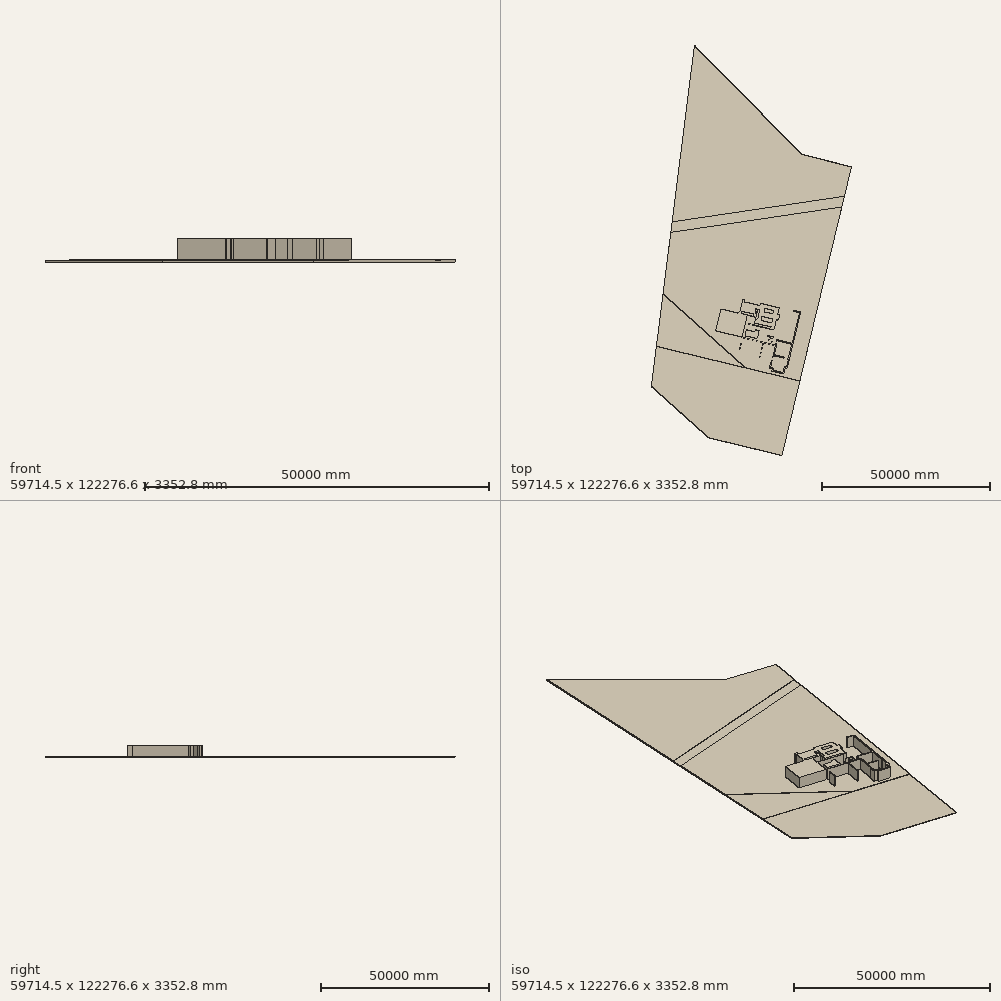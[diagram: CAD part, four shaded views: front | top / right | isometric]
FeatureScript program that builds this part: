
annotation { "Feature Type Name" : "Feature", "Feature Type Description" : "" }
export const myFeature = defineFeature(function(context is Context, id is Id, definition is map)
    precondition{}
    {
        {
            var Q0;
            Q0=qCreatedBy(makeId("Top.planeOp"),FACE);
            var sketch = newSketch(context, id + "F0", { "sketchPlane" : qUnion([Q0])});
            skLineSegment(sketch, "E0", {"start": v(0, 0) * mm, "end": v(31989.83, -32467.96) * mm});
            skLineSegment(sketch, "E1", {"start": v(31989.83, -32467.96) * mm, "end": v(46862.18, -36229.17) * mm});
            skLineSegment(sketch, "E2", {"start": v(46862.18, -36229.17) * mm, "end": v(26112.23, -122276.56) * mm});
            skLineSegment(sketch, "E3", {"start": v(46862.18, -36229.17) * mm, "end": v(46862.18, -51469.17) * mm, "construction": true});
            skLineSegment(sketch, "E4", {"start": v(0, 0) * mm, "end": v(-12852.3, -101676.89) * mm});
            skLineSegment(sketch, "E5", {"start": v(0, 0) * mm, "end": v(0, 15240) * mm, "construction": true});
            skLineSegment(sketch, "E6", {"start": v(26112.23, -122276.56) * mm, "end": v(4230, -116999.76) * mm});
            skLineSegment(sketch, "E7", {"start": v(26112.23, -122276.56) * mm, "end": v(10872.23, -122276.56) * mm, "construction": true});
            skLineSegment(sketch, "E8", {"start": v(4230, -116999.76) * mm, "end": v(-12852.3, -101676.89) * mm});
            skArc(sketch, "E9", {"start": v(-4165.07, -109469.35) * mm, "mid": v(-689.73, -114039.67) * mm, "end": v(4230, -116999.76) * mm, "construction": true});
            skArc(sketch, "E10", {"start": v(-4165.07, -109469.35) * mm, "mid": v(-8132.26, -105153.47) * mm, "end": v(-12852.3, -101676.89) * mm, "construction": true});
            skLineSegment(sketch, "E11", {"start": v(31471.2, -100053.58) * mm, "end": v(-11342.08, -89729.35) * mm});
            skLineSegment(sketch, "E12", {"start": v(-9365.85, -74095.03) * mm, "end": v(15198.72, -96129.54) * mm});
            skLineSegment(sketch, "E13", {"start": v(-6651.63, -52622.31) * mm, "end": v(44754.67, -44968.73) * mm});
            skLineSegment(sketch, "E14", {"start": v(-7048.63, -55763.02) * mm, "end": v(43983.88, -48165.09) * mm});
            skSolve(sketch);
        }
        {
            var Q0;
            {var subQ4=sQuery(id+"F0.wireOp",EDGE,"E0");Q0=makeQuery(id+"F0.imprint","IMPRINT",FACE,{"disambiguationData":[TD([[makeQuery(id+"F0.imprint","IMPRINT",EDGE,{"derivedFrom":subQ4}),-1.0]])]});}
            var Q1;
            {var subQ0=sQuery(id+"F0.wireOp",EDGE,"E13");Q1=makeQuery(id+"F0.imprint","IMPRINT",FACE,{"disambiguationData":[TD([[makeQuery(id+"F0.imprint","IMPRINT",EDGE,{"derivedFrom":subQ0}),-1.0]])]});}
            var Q2;
            {var subQ0=sQuery(id+"F0.wireOp",EDGE,"E12");Q2=makeQuery(id+"F0.imprint","IMPRINT",FACE,{"disambiguationData":[TD([[makeQuery(id+"F0.imprint","IMPRINT",EDGE,{"derivedFrom":subQ0}),1.0]])]});}
            var Q3;
            {var subQ3=sQuery(id+"F0.wireOp",EDGE,"E12");Q3=makeQuery(id+"F0.imprint","IMPRINT",FACE,{"disambiguationData":[TD([[makeQuery(id+"F0.imprint","IMPRINT",EDGE,{"derivedFrom":subQ3}),-1.0]])]});}
            var Q4;
            {var subQ1=sQuery(id+"F0.wireOp",EDGE,"E6");Q4=makeQuery(id+"F0.imprint","IMPRINT",FACE,{"disambiguationData":[TD([[makeQuery(id+"F0.imprint","IMPRINT",EDGE,{"derivedFrom":subQ1}),-1.0]])]});}
            extrude(context, id + "F1", {"entities" : qUnion([Q0, Q1, Q2, Q3, Q4]), "depth" : 304.8 * mm, "offsetDistance" : 25.4 * mm});
        }
        {
            var Q0;
            Q0=makeQuery(id+"F1.opExtrude","CAP_FACE",FACE,{"disambiguationData":[OSD([sQuery(id+"F0.wireOp",EDGE,"E0"),sQuery(id+"F0.wireOp",EDGE,"E1"),sQuery(id+"F0.wireOp",EDGE,"E2"),sQuery(id+"F0.wireOp",EDGE,"E4"),sQuery(id+"F0.wireOp",EDGE,"E6"),sQuery(id+"F0.wireOp",EDGE,"E8")])],"isStart":false});
            var sketch = newSketch(context, id + "F2", { "sketchPlane" : qUnion([Q0])});
            skLineSegment(sketch, "E15.0", {"start": v(-9365.85, -74095.03) * mm, "end": v(15198.72, -96129.54) * mm});
            skLineSegment(sketch, "E16.0", {"start": v(31471.2, -100053.58) * mm, "end": v(-11342.08, -89729.35) * mm});
            skLineSegment(sketch, "E17.0", {"start": v(0, 0) * mm, "end": v(-12852.3, -101676.89) * mm});
            skSolve(sketch);
        }
        {
            var Q0;
            {var subQ0=sQuery(id+"F2.wireOp",EDGE,"E15.0");Q0=makeQuery(id+"F2.imprint","IMPRINT",FACE,{"disambiguationData":[TD([[makeQuery(id+"F2.imprint","IMPRINT",EDGE,{"derivedFrom":subQ0}),-1.0]])]});}
            extrude(context, id + "F3", {"entities" : qUnion([Q0]), "operationType" : NewBodyOperationType.REMOVE, "oppositeDirection" : true, "depth" : 76.2 * mm, "offsetDistance" : 25.4 * mm});
        }
        {
            var Q0;
            Q0=makeQuery(id+"F1.opExtrude","CAP_FACE",FACE,{"disambiguationData":[OSD([sQuery(id+"F0.wireOp",EDGE,"E0"),sQuery(id+"F0.wireOp",EDGE,"E1"),sQuery(id+"F0.wireOp",EDGE,"E2"),sQuery(id+"F0.wireOp",EDGE,"E4"),sQuery(id+"F0.wireOp",EDGE,"E6"),sQuery(id+"F0.wireOp",EDGE,"E8")])],"isStart":false});
            var sketch = newSketch(context, id + "F4", { "sketchPlane" : qUnion([Q0])});
            skLineSegment(sketch, "E18.0", {"start": v(0, 0) * mm, "end": v(-12852.3, -101676.89) * mm});
            skLineSegment(sketch, "E19.0", {"start": v(4230, -116999.76) * mm, "end": v(-12852.3, -101676.89) * mm});
            skLineSegment(sketch, "E20.0", {"start": v(26112.23, -122276.56) * mm, "end": v(4230, -116999.76) * mm});
            skLineSegment(sketch, "E21.0", {"start": v(46862.18, -36229.17) * mm, "end": v(26112.23, -122276.56) * mm});
            skLineSegment(sketch, "E22.0", {"start": v(31471.2, -100053.58) * mm, "end": v(-11342.08, -89729.35) * mm});
            skSolve(sketch);
        }
        {
            var Q0;
            {var subQ4=sQuery(id+"F4.wireOp",EDGE,"E19.0");Q0=makeQuery(id+"F4.imprint","IMPRINT",FACE,{"disambiguationData":[TD([[makeQuery(id+"F4.imprint","IMPRINT",EDGE,{"derivedFrom":subQ4}),-1.0]])]});}
            extrude(context, id + "F5", {"entities" : qUnion([Q0]), "operationType" : NewBodyOperationType.REMOVE, "oppositeDirection" : true, "depth" : 152.4 * mm, "offsetDistance" : 25.4 * mm});
        }
        {
            var Q0;
            Q0=makeQuery(id+"F1.opExtrude","CAP_FACE",FACE,{"disambiguationData":[OSD([sQuery(id+"F0.wireOp",EDGE,"E0"),sQuery(id+"F0.wireOp",EDGE,"E1"),sQuery(id+"F0.wireOp",EDGE,"E2"),sQuery(id+"F0.wireOp",EDGE,"E4"),sQuery(id+"F0.wireOp",EDGE,"E6"),sQuery(id+"F0.wireOp",EDGE,"E8")])],"isStart":false});
            var sketch = newSketch(context, id + "F6", { "sketchPlane" : qUnion([Q0])});
            skLineSegment(sketch, "E23.0", {"start": v(-6651.63, -52622.31) * mm, "end": v(44754.67, -44968.73) * mm});
            skLineSegment(sketch, "E24.0", {"start": v(-7048.63, -55763.02) * mm, "end": v(43983.88, -48165.09) * mm});
            skLineSegment(sketch, "E25.0", {"start": v(0, 0) * mm, "end": v(-12852.3, -101676.89) * mm});
            skLineSegment(sketch, "E26.0", {"start": v(46862.18, -36229.17) * mm, "end": v(26112.23, -122276.56) * mm});
            skSolve(sketch);
        }
        {
            var Q0;
            {var subQ0=sQuery(id+"F6.wireOp",EDGE,"E23.0");Q0=makeQuery(id+"F6.imprint","IMPRINT",FACE,{"disambiguationData":[TD([[makeQuery(id+"F6.imprint","IMPRINT",EDGE,{"derivedFrom":subQ0}),-1.0]])]});}
            extrude(context, id + "F7", {"entities" : qUnion([Q0]), "operationType" : NewBodyOperationType.REMOVE, "oppositeDirection" : true, "depth" : 152.4 * mm, "offsetDistance" : 25.4 * mm});
        }
        {
            var Q0;
            {var subQ0=sQuery(id+"F0.wireOp",EDGE,"E4");var subQ1=sQuery(id+"F0.wireOp",EDGE,"E2");Q0=makeQuery(id+"F7.boolean.opBoolean","SPLIT",FACE,{"disambiguationData":[TD([makeQuery(id+"F3.boolean.opBoolean","COPY",FACE,{"derivedFrom":makeQuery(id+"F3.opExtrude","SWEPT_FACE",FACE,{"disambiguationData":[OSD([sQuery(id+"F2.wireOp",EDGE,"E15.0")])]})})])],"derivedFrom":makeQuery(id+"F1.opExtrude","CAP_FACE",FACE,{"disambiguationData":[OSD([sQuery(id+"F0.wireOp",EDGE,"E0"),sQuery(id+"F0.wireOp",EDGE,"E1"),subQ1,subQ0,sQuery(id+"F0.wireOp",EDGE,"E6"),sQuery(id+"F0.wireOp",EDGE,"E8")])],"isStart":false})});}
            var sketch = newSketch(context, id + "F8", { "sketchPlane" : qUnion([Q0])});
            skLineSegment(sketch, "E27", {"start": v(27669.68, -96315.03) * mm, "end": v(31724.64, -79499.64) * mm});
            skPoint(sketch, "E28.orphan", {"position": v(31471.2, -100053.58) * mm});
            skLineSegment(sketch, "E29", {"start": v(-5717.12, -79311.3) * mm, "end": v(3764.68, -81597.8) * mm});
            skLineSegment(sketch, "E30", {"start": v(3764.68, -81597.8) * mm, "end": v(7766.05, -65004.64) * mm});
            skLineSegment(sketch, "E31", {"start": v(7766.05, -65004.64) * mm, "end": v(-1715.76, -62718.14) * mm});
            skLineSegment(sketch, "E32", {"start": v(-1715.76, -62718.14) * mm, "end": v(-5717.12, -79311.3) * mm});
            skLineSegment(sketch, "E33", {"start": v(-5145.5, -76940.85) * mm, "end": v(-2182.44, -77655.38) * mm});
            skLineSegment(sketch, "E34", {"start": v(-2182.44, -77655.38) * mm, "end": v(-2754.06, -80025.83) * mm});
            skLineSegment(sketch, "E35", {"start": v(-5145.5, -76940.85) * mm, "end": v(-9590.1, -75869.05) * mm});
            skLineSegment(sketch, "E36", {"start": v(-2182.44, -77655.38) * mm, "end": v(1247.3, -63432.67) * mm});
            skLineSegment(sketch, "E37", {"start": v(3764.68, -81597.8) * mm, "end": v(7190.64, -82423.95) * mm});
            skLineSegment(sketch, "E38", {"start": v(4934.3, -91780.7) * mm, "end": v(-10343.91, -88096.42) * mm});
            skLineSegment(sketch, "E39.0", {"start": v(4230, -116999.76) * mm, "end": v(-12852.3, -101676.89) * mm});
            skLineSegment(sketch, "E40", {"start": v(-2047.33, -90097.1) * mm, "end": v(-6264.7, -107585.98) * mm});
            skLineSegment(sketch, "E41", {"start": v(-5603, -89239.67) * mm, "end": v(-9358.03, -104811.25) * mm});
            skArc(sketch, "E42", {"start": v(-6746.26, -93980.57) * mm, "mid": v(-7326.44, -90293.4) * mm, "end": v(-10343.91, -88096.42) * mm});
            skLineSegment(sketch, "E43", {"start": v(-8087.58, -78739.68) * mm, "end": v(-10343.91, -88096.42) * mm});
            skLineSegment(sketch, "E44", {"start": v(-5717.12, -79311.3) * mm, "end": v(-8087.58, -78739.68) * mm});
            skLineSegment(sketch, "E45", {"start": v(22775.38, -94507.71) * mm, "end": v(22346.66, -96285.55) * mm});
            skLineSegment(sketch, "E46", {"start": v(22346.66, -96285.55) * mm, "end": v(23235.58, -96499.91) * mm});
            skLineSegment(sketch, "E47", {"start": v(23235.58, -96499.91) * mm, "end": v(23092.67, -97092.52) * mm});
            skLineSegment(sketch, "E48", {"start": v(23092.67, -97092.52) * mm, "end": v(26648.35, -97949.96) * mm});
            skLineSegment(sketch, "E49", {"start": v(26648.35, -97949.96) * mm, "end": v(27077.07, -96172.12) * mm});
            skLineSegment(sketch, "E50", {"start": v(13071.34, -92167.63) * mm, "end": v(14241.39, -87315.61) * mm});
            skLineSegment(sketch, "E51", {"start": v(14241.39, -87315.61) * mm, "end": v(5985.04, -85324.63) * mm});
            skLineSegment(sketch, "E52", {"start": v(5985.04, -85324.63) * mm, "end": v(7699.91, -78213.28) * mm});
            skLineSegment(sketch, "E53", {"start": v(14020.33, -75230.32) * mm, "end": v(31724.64, -79499.64) * mm});
            skLineSegment(sketch, "E54.trimOffspring", {"start": v(27077.07, -96172.12) * mm, "end": v(27669.68, -96315.03) * mm});
            skLineSegment(sketch, "E55.0", {"start": v(6352.8, -85099.78) * mm, "end": v(7924.77, -78581.03) * mm});
            skLineSegment(sketch, "E55.1", {"start": v(23460.43, -96867.67) * mm, "end": v(26423.5, -97582.2) * mm});
            skLineSegment(sketch, "E55.2", {"start": v(26423.5, -97582.2) * mm, "end": v(26852.22, -95804.36) * mm});
            skLineSegment(sketch, "E55.3", {"start": v(26852.22, -95804.36) * mm, "end": v(27444.83, -95947.27) * mm});
            skLineSegment(sketch, "E55.4", {"start": v(27444.83, -95947.27) * mm, "end": v(28016.45, -93576.82) * mm});
            skLineSegment(sketch, "E55.5", {"start": v(23603.34, -96275.06) * mm, "end": v(23460.43, -96867.67) * mm});
            skLineSegment(sketch, "E55.6", {"start": v(14245.18, -75598.08) * mm, "end": v(19282.4, -76812.78) * mm});
            skLineSegment(sketch, "E55.7", {"start": v(22714.42, -96060.7) * mm, "end": v(23603.34, -96275.06) * mm});
            skLineSegment(sketch, "E55.8", {"start": v(23143.14, -94282.86) * mm, "end": v(22714.42, -96060.7) * mm});
            skLineSegment(sketch, "E55.9", {"start": v(13439.1, -91942.77) * mm, "end": v(23143.14, -94282.86) * mm});
            skLineSegment(sketch, "E55.10", {"start": v(13439.1, -91942.77) * mm, "end": v(14609.14, -87090.76) * mm});
            skLineSegment(sketch, "E55.11", {"start": v(14609.14, -87090.76) * mm, "end": v(6352.8, -85099.78) * mm});
            skLineSegment(sketch, "E56", {"start": v(14609.14, -87090.76) * mm, "end": v(19350.05, -88234) * mm});
            skLineSegment(sketch, "E57", {"start": v(20619.6, -88657.73) * mm, "end": v(19476.35, -93398.63) * mm});
            skLineSegment(sketch, "E58.0", {"start": v(20508.48, -88630.93) * mm, "end": v(19365.23, -93371.83) * mm});
            skLineSegment(sketch, "E58.1", {"start": v(14582.35, -87201.87) * mm, "end": v(20508.48, -88630.93) * mm});
            skLineSegment(sketch, "E59", {"start": v(17710.43, -83331.52) * mm, "end": v(18255.26, -81072.19) * mm});
            skLineSegment(sketch, "E60", {"start": v(17821.54, -83358.32) * mm, "end": v(18964.79, -78617.41) * mm});
            skLineSegment(sketch, "E61", {"start": v(7924.77, -78581.03) * mm, "end": v(18255.26, -81072.19) * mm});
            skLineSegment(sketch, "E62", {"start": v(14020.33, -75230.32) * mm, "end": v(12993.2, -79489.73) * mm});
            skLineSegment(sketch, "E63", {"start": v(12993.2, -79489.73) * mm, "end": v(7699.91, -78213.28) * mm});
            skLineSegment(sketch, "E64", {"start": v(14245.18, -75598.08) * mm, "end": v(13218.05, -79857.49) * mm});
            skLineSegment(sketch, "E65", {"start": v(13244.84, -79746.37) * mm, "end": v(18282.05, -80961.07) * mm});
            skLineSegment(sketch, "E66", {"start": v(23143.14, -94282.86) * mm, "end": v(23571.86, -92505.02) * mm});
            skLineSegment(sketch, "E67", {"start": v(24202.07, -89404.05) * mm, "end": v(19350.05, -88234) * mm});
            skLineSegment(sketch, "E68", {"start": v(23032.02, -94256.07) * mm, "end": v(24175.27, -89515.16) * mm});
            skLineSegment(sketch, "E69", {"start": v(24175.27, -89515.16) * mm, "end": v(20619.6, -88657.73) * mm});
            skLineSegment(sketch, "E70", {"start": v(19833.61, -91917.1) * mm, "end": v(21018.84, -92202.9) * mm});
            skLineSegment(sketch, "E71", {"start": v(21018.84, -92202.9) * mm, "end": v(21519, -90128.76) * mm});
            skLineSegment(sketch, "E72", {"start": v(21519, -90128.76) * mm, "end": v(23889.46, -90700.39) * mm});
            skLineSegment(sketch, "E73", {"start": v(23571.86, -92505.02) * mm, "end": v(28016.45, -93576.82) * mm});
            skLineSegment(sketch, "E74", {"start": v(23828.5, -92253.37) * mm, "end": v(27982.96, -93255.2) * mm});
            skLineSegment(sketch, "E75.trimOffspring", {"start": v(18282.05, -80961.07) * mm, "end": v(18853.67, -78590.62) * mm});
            skLineSegment(sketch, "E76", {"start": v(28983.3, -89106.91) * mm, "end": v(24828.84, -88105.08) * mm});
            skLineSegment(sketch, "E77", {"start": v(27982.96, -93255.2) * mm, "end": v(28983.3, -89106.91) * mm});
            skLineSegment(sketch, "E78", {"start": v(23828.5, -92253.37) * mm, "end": v(24828.84, -88105.08) * mm});
            skLineSegment(sketch, "E79.trimOffspring", {"start": v(29159.7, -88835.91) * mm, "end": v(31356.88, -79724.5) * mm});
            skLineSegment(sketch, "E80", {"start": v(29159.7, -88835.91) * mm, "end": v(24603.99, -87737.32) * mm});
            skLineSegment(sketch, "E81", {"start": v(24603.99, -87737.32) * mm, "end": v(24202.07, -89404.05) * mm});
            skLineSegment(sketch, "E82", {"start": v(26023.36, -78438.34) * mm, "end": v(24951.57, -82882.93) * mm});
            skLineSegment(sketch, "E83", {"start": v(24951.57, -82882.93) * mm, "end": v(30285.09, -84169.09) * mm});
            skLineSegment(sketch, "E84", {"start": v(25912.25, -78411.54) * mm, "end": v(24340.28, -84930.28) * mm});
            skLineSegment(sketch, "E85", {"start": v(24924.77, -82994.05) * mm, "end": v(30258.3, -84280.2) * mm});
            skLineSegment(sketch, "E86", {"start": v(21057.5, -78390.48) * mm, "end": v(23724.26, -79033.55) * mm});
            skLineSegment(sketch, "E87", {"start": v(23724.26, -79033.55) * mm, "end": v(23474.18, -80070.63) * mm});
            skLineSegment(sketch, "E88", {"start": v(23474.18, -80070.63) * mm, "end": v(20807.42, -79427.55) * mm});
            skLineSegment(sketch, "E89", {"start": v(20807.42, -79427.55) * mm, "end": v(21057.5, -78390.48) * mm});
            skLineSegment(sketch, "E90", {"start": v(12993.2, -79489.73) * mm, "end": v(12921.74, -79786.03) * mm});
            skLineSegment(sketch, "E91", {"start": v(17821.54, -83358.32) * mm, "end": v(24340.28, -84930.28) * mm});
            skLineSegment(sketch, "E92", {"start": v(25961.85, -83244.13) * mm, "end": v(25553.97, -84935.55) * mm});
            skLineSegment(sketch, "E93", {"start": v(15313.18, -82871.01) * mm, "end": v(24424.6, -85068.2) * mm});
            skLineSegment(sketch, "E94", {"start": v(24424.6, -85068.2) * mm, "end": v(24924.77, -82994.05) * mm});
            skLineSegment(sketch, "E95", {"start": v(25054.81, -81967.22) * mm, "end": v(24462.2, -81824.31) * mm});
            skLineSegment(sketch, "E96", {"start": v(24462.2, -81824.31) * mm, "end": v(23747.67, -84787.38) * mm});
            skLineSegment(sketch, "E97", {"start": v(22853.5, -83944.68) * mm, "end": v(17964.45, -82765.7) * mm});
            skLineSegment(sketch, "E98", {"start": v(18807.15, -81871.54) * mm, "end": v(19557.4, -78760.32) * mm});
            skLineSegment(sketch, "E99", {"start": v(19557.4, -78760.32) * mm, "end": v(18964.79, -78617.41) * mm});
            skLineSegment(sketch, "E100", {"start": v(20165.76, -80788.24) * mm, "end": v(19879.94, -81973.47) * mm});
            skLineSegment(sketch, "E101", {"start": v(19879.94, -81973.47) * mm, "end": v(23139.32, -82759.45) * mm});
            skLineSegment(sketch, "E102", {"start": v(23139.32, -82759.45) * mm, "end": v(23425.13, -81574.23) * mm});
            skLineSegment(sketch, "E103", {"start": v(23425.13, -81574.23) * mm, "end": v(20165.76, -80788.24) * mm});
            skLineSegment(sketch, "E104", {"start": v(19282.4, -76812.78) * mm, "end": v(25912.25, -78411.54) * mm});
            skLineSegment(sketch, "E105.trimOffspring", {"start": v(26023.36, -78438.34) * mm, "end": v(31356.88, -79724.5) * mm});
            skLineSegment(sketch, "E106", {"start": v(27837.43, -93533.65) * mm, "end": v(27908.89, -93237.34) * mm});
            skLineSegment(sketch, "E107", {"start": v(26948.51, -93319.29) * mm, "end": v(27019.97, -93022.98) * mm});
            skLineSegment(sketch, "E108", {"start": v(26972.33, -93220.52) * mm, "end": v(27861.25, -93434.88) * mm});
            skLineSegment(sketch, "E109", {"start": v(26963.4, -93257.56) * mm, "end": v(27852.32, -93471.92) * mm});
            skLineSegment(sketch, "E110", {"start": v(24810.98, -88179.16) * mm, "end": v(24514.67, -88107.7) * mm});
            skLineSegment(sketch, "E111", {"start": v(24300.31, -88996.63) * mm, "end": v(24596.62, -89068.08) * mm});
            skLineSegment(sketch, "E112", {"start": v(24362.04, -89011.51) * mm, "end": v(24576.4, -88122.6) * mm});
            skLineSegment(sketch, "E113", {"start": v(24399.08, -89020.44) * mm, "end": v(24613.44, -88131.52) * mm});
            skLineSegment(sketch, "E114", {"start": v(23016.84, -89118.24) * mm, "end": v(23543.8, -86932.98) * mm});
            skLineSegment(sketch, "E115", {"start": v(22905.73, -89091.44) * mm, "end": v(23405.9, -87017.3) * mm});
            skLineSegment(sketch, "E116", {"start": v(15884.8, -80500.56) * mm, "end": v(14312.84, -87019.3) * mm});
            skLineSegment(sketch, "E117", {"start": v(15339.97, -82759.9) * mm, "end": v(17710.43, -83331.52) * mm});
            skLineSegment(sketch, "E118", {"start": v(18807.15, -81871.54) * mm, "end": v(18214.53, -81728.63) * mm});
            skLineSegment(sketch, "E119", {"start": v(13071.34, -92167.63) * mm, "end": v(23071.68, -94579.17) * mm});
            skLineSegment(sketch, "E120", {"start": v(19247.36, -85896.9) * mm, "end": v(23543.8, -86932.98) * mm});
            skLineSegment(sketch, "E121", {"start": v(19109.45, -85981.23) * mm, "end": v(19739.1, -86133.06) * mm});
            skLineSegment(sketch, "E122", {"start": v(22016.8, -88877.08) * mm, "end": v(22516.98, -86802.94) * mm});
            skLineSegment(sketch, "E123", {"start": v(21905.7, -88850.29) * mm, "end": v(22405.86, -86776.14) * mm});
            skLineSegment(sketch, "E124", {"start": v(20090.81, -88412.64) * mm, "end": v(20590.98, -86338.5) * mm});
            skLineSegment(sketch, "E125", {"start": v(20201.93, -88439.43) * mm, "end": v(20702.1, -86365.29) * mm});
            skLineSegment(sketch, "E126", {"start": v(20344.83, -87846.82) * mm, "end": v(22048.6, -88257.67) * mm});
            skCircle(sketch, "E127", {"center": v(20717.84, -88250.3) * mm, "radius": 152.4 * mm});
            skCircle(sketch, "E128", {"center": v(21532.68, -88446.8) * mm, "radius": 152.4 * mm});
            skLineSegment(sketch, "E129", {"start": v(19473.5, -88263.78) * mm, "end": v(19544.96, -87967.47) * mm});
            skLineSegment(sketch, "E130", {"start": v(19544.96, -87967.47) * mm, "end": v(20038.8, -88086.56) * mm});
            skLineSegment(sketch, "E131", {"start": v(20038.8, -88086.56) * mm, "end": v(19967.35, -88382.87) * mm});
            skLineSegment(sketch, "E132", {"start": v(19643.73, -87991.29) * mm, "end": v(19756.86, -87522.14) * mm});
            skLineSegment(sketch, "E133", {"start": v(19756.86, -87522.14) * mm, "end": v(20053.17, -87593.59) * mm});
            skLineSegment(sketch, "E134", {"start": v(20053.17, -87593.59) * mm, "end": v(19940.04, -88062.74) * mm});
            skLineSegment(sketch, "E135", {"start": v(19760.9, -86530.24) * mm, "end": v(20501.67, -86708.88) * mm});
            skLineSegment(sketch, "E136", {"start": v(20600.87, -86785.05) * mm, "end": v(20489.76, -86758.26) * mm});
            skLineSegment(sketch, "E137", {"start": v(20346.85, -87350.87) * mm, "end": v(20457.97, -87377.67) * mm});
            skLineSegment(sketch, "E138", {"start": v(20402.41, -87364.27) * mm, "end": v(20545.32, -86771.66) * mm});
            skArc(sketch, "E139", {"start": v(20402.41, -87364.27) * mm, "mid": v(20012.42, -87067.68) * mm, "end": v(19966.67, -86579.86) * mm, "construction": true});
            skLineSegment(sketch, "E140", {"start": v(22231.16, -87988.16) * mm, "end": v(23120.08, -88202.52) * mm});
            skLineSegment(sketch, "E141", {"start": v(23120.08, -88202.52) * mm, "end": v(22016.8, -88877.08) * mm});
            skLineSegment(sketch, "E142", {"start": v(22231.16, -87988.16) * mm, "end": v(22905.73, -89091.44) * mm});
            skCircle(sketch, "E143", {"center": v(22568.44, -88539.8) * mm, "radius": 50.8 * mm});
            skLineSegment(sketch, "E144", {"start": v(22427.66, -87173.32) * mm, "end": v(23316.58, -87387.68) * mm});
            skLineSegment(sketch, "E145", {"start": v(22304.64, -87195.9) * mm, "end": v(22415.75, -87222.7) * mm});
            skLineSegment(sketch, "E146", {"start": v(22161.73, -87788.52) * mm, "end": v(22272.85, -87815.32) * mm});
            skLineSegment(sketch, "E147", {"start": v(22360.2, -87209.3) * mm, "end": v(22217.29, -87801.92) * mm});
            skArc(sketch, "E148", {"start": v(22217.29, -87801.92) * mm, "mid": v(22699.6, -87715.68) * mm, "end": v(22962.65, -87302.33) * mm, "construction": true});
            skLineSegment(sketch, "E149", {"start": v(19461.72, -85007.99) * mm, "end": v(21239.56, -85436.7) * mm});
            skLineSegment(sketch, "E150", {"start": v(19390.27, -85304.3) * mm, "end": v(21168.1, -85733.01) * mm});
            skLineSegment(sketch, "E151", {"start": v(20612.78, -86735.67) * mm, "end": v(20909.09, -86807.12) * mm});
            skLineSegment(sketch, "E152", {"start": v(21239.56, -85436.7) * mm, "end": v(21025.2, -86325.63) * mm});
            skLineSegment(sketch, "E153", {"start": v(21980.33, -85615.34) * mm, "end": v(21765.97, -86504.26) * mm});
            skLineSegment(sketch, "E154", {"start": v(21099.28, -86343.49) * mm, "end": v(21072.48, -86454.6) * mm});
            skLineSegment(sketch, "E155", {"start": v(21691.9, -86486.4) * mm, "end": v(21665.1, -86597.5) * mm});
            skLineSegment(sketch, "E156", {"start": v(21085.88, -86399.05) * mm, "end": v(21678.5, -86541.95) * mm});
            skLineSegment(sketch, "E157", {"start": v(20909.09, -86807.12) * mm, "end": v(20998.4, -86436.74) * mm});
            skLineSegment(sketch, "E158", {"start": v(21649.86, -86985.76) * mm, "end": v(21739.17, -86615.37) * mm});
            skLineSegment(sketch, "E159.trimOffspring", {"start": v(21649.86, -86985.76) * mm, "end": v(22316.55, -87146.52) * mm});
            skLineSegment(sketch, "E160.trimOffspring", {"start": v(21908.87, -85911.64) * mm, "end": v(23686.71, -86340.36) * mm});
            skLineSegment(sketch, "E161.trimOffspring", {"start": v(21980.33, -85615.34) * mm, "end": v(23758.16, -86044.06) * mm});
            skLineSegment(sketch, "E162", {"start": v(15482.88, -82167.29) * mm, "end": v(17853.33, -82738.9) * mm});
            skLineSegment(sketch, "E163", {"start": v(15741.9, -81093.17) * mm, "end": v(18112.35, -81664.8) * mm});
            skLineSegment(sketch, "E164", {"start": v(17889.06, -82590.76) * mm, "end": v(18000.17, -82617.55) * mm});
            skLineSegment(sketch, "E165", {"start": v(18067.7, -81850) * mm, "end": v(18178.8, -81876.79) * mm});
            skLineSegment(sketch, "E166", {"start": v(18123.25, -81863.39) * mm, "end": v(17944.62, -82604.15) * mm});
            skLineSegment(sketch, "E167", {"start": v(15397.07, -82035.55) * mm, "end": v(15508.19, -82062.34) * mm});
            skLineSegment(sketch, "E168", {"start": v(15611.43, -81146.63) * mm, "end": v(15722.55, -81173.42) * mm});
            skLineSegment(sketch, "E169", {"start": v(15666.99, -81160.03) * mm, "end": v(15452.63, -82048.95) * mm});
            skLineSegment(sketch, "E170", {"start": v(22853.5, -83944.68) * mm, "end": v(22710.6, -84537.3) * mm});
            skLineSegment(sketch, "E171", {"start": v(22784.67, -84555.16) * mm, "end": v(22757.88, -84666.27) * mm});
            skLineSegment(sketch, "E172", {"start": v(23673.6, -84769.51) * mm, "end": v(23646.8, -84880.63) * mm});
            skLineSegment(sketch, "E173", {"start": v(25412.08, -80485.69) * mm, "end": v(24708.35, -80315.99) * mm});
            skLineSegment(sketch, "E174", {"start": v(24708.35, -80315.99) * mm, "end": v(25208.52, -78241.84) * mm});
            skLineSegment(sketch, "E175", {"start": v(18853.67, -78590.62) * mm, "end": v(18964.79, -78617.41) * mm});
            skLineSegment(sketch, "E176", {"start": v(25319.64, -78268.64) * mm, "end": v(24846.26, -80231.67) * mm});
            skLineSegment(sketch, "E177", {"start": v(24846.26, -80231.67) * mm, "end": v(25438.87, -80374.57) * mm});
            skLineSegment(sketch, "E178", {"start": v(26072.96, -83270.93) * mm, "end": v(25665.08, -84962.34) * mm});
            skLineSegment(sketch, "E179", {"start": v(25715.7, -84752.46) * mm, "end": v(29901.03, -85761.73) * mm});
            skLineSegment(sketch, "E180", {"start": v(25688.9, -84863.58) * mm, "end": v(29874.23, -85872.85) * mm});
            skLineSegment(sketch, "E181", {"start": v(28554.53, -83869.35) * mm, "end": v(28197.26, -85350.88) * mm});
            skLineSegment(sketch, "E182", {"start": v(28443.41, -83842.55) * mm, "end": v(28086.15, -85324.08) * mm});
            skLineSegment(sketch, "E183", {"start": v(27702.65, -83663.92) * mm, "end": v(27345.38, -85145.45) * mm});
            skLineSegment(sketch, "E184", {"start": v(25941.96, -83814.16) * mm, "end": v(26830.88, -84028.52) * mm});
            skLineSegment(sketch, "E185", {"start": v(26830.88, -84028.52) * mm, "end": v(26961.88, -83485.29) * mm});
            skLineSegment(sketch, "E186", {"start": v(27085.34, -83515.06) * mm, "end": v(27013.89, -83811.37) * mm});
            skLineSegment(sketch, "E187", {"start": v(27013.89, -83811.37) * mm, "end": v(27507.73, -83930.45) * mm});
            skLineSegment(sketch, "E188", {"start": v(27507.73, -83930.45) * mm, "end": v(27579.19, -83634.15) * mm});
            skLineSegment(sketch, "E189", {"start": v(27112.66, -83835.18) * mm, "end": v(26999.52, -84304.34) * mm});
            skLineSegment(sketch, "E190", {"start": v(26999.52, -84304.34) * mm, "end": v(27295.83, -84375.79) * mm});
            skLineSegment(sketch, "E191", {"start": v(27295.83, -84375.79) * mm, "end": v(27408.96, -83906.64) * mm});
            skLineSegment(sketch, "E192", {"start": v(25762.98, -84881.44) * mm, "end": v(25789.77, -84770.32) * mm});
            skLineSegment(sketch, "E193", {"start": v(26355.6, -85024.34) * mm, "end": v(26382.39, -84913.23) * mm});
            skLineSegment(sketch, "E194", {"start": v(25776.38, -84825.88) * mm, "end": v(26368.99, -84968.79) * mm});
            skArc(sketch, "E195", {"start": v(26368.99, -84968.79) * mm, "mid": v(26275.53, -84475.95) * mm, "end": v(25844.08, -84220.05) * mm, "construction": true});
            skLineSegment(sketch, "E196", {"start": v(28340.17, -84758.27) * mm, "end": v(30043.93, -85169.12) * mm});
            skLineSegment(sketch, "E197", {"start": v(28366.96, -84647.15) * mm, "end": v(30070.73, -85058) * mm});
            skLineSegment(sketch, "E198", {"start": v(29278.79, -88342.07) * mm, "end": v(27303.41, -87865.72) * mm});
            skLineSegment(sketch, "E199", {"start": v(27303.41, -87865.72) * mm, "end": v(27755.95, -85989.1) * mm});
            skLineSegment(sketch, "E200", {"start": v(27755.95, -85989.1) * mm, "end": v(29731.32, -86465.46) * mm});
            skLineSegment(sketch, "E201", {"start": v(28296.03, -85374.7) * mm, "end": v(28269.24, -85485.81) * mm});
            skLineSegment(sketch, "E202", {"start": v(29777.56, -85731.96) * mm, "end": v(29750.77, -85843.08) * mm});
            skLineSegment(sketch, "E203", {"start": v(29036.8, -85553.33) * mm, "end": v(29010, -85664.44) * mm});
            skLineSegment(sketch, "E204", {"start": v(28282.63, -85430.25) * mm, "end": v(29023.4, -85608.89) * mm});
            skLineSegment(sketch, "E205", {"start": v(29023.4, -85608.89) * mm, "end": v(29764.17, -85787.52) * mm});
            skArc(sketch, "E206", {"start": v(25137.16, -86664) * mm, "mid": v(24733.67, -87037.01) * mm, "end": v(24922.8, -87552.92) * mm});
            skLineSegment(sketch, "E207", {"start": v(26429.67, -85042.2) * mm, "end": v(26197.45, -86005.2) * mm});
            skLineSegment(sketch, "E208", {"start": v(26197.45, -86005.2) * mm, "end": v(25456.68, -85826.57) * mm});
            skLineSegment(sketch, "E209", {"start": v(26540.78, -85069) * mm, "end": v(26281.77, -86143.11) * mm});
            skLineSegment(sketch, "E210", {"start": v(26281.77, -86143.11) * mm, "end": v(25429.88, -85937.69) * mm});
            skLineSegment(sketch, "E211", {"start": v(26405.85, -85140.98) * mm, "end": v(26516.97, -85167.77) * mm});
            skLineSegment(sketch, "E212", {"start": v(26215.3, -85931.13) * mm, "end": v(26326.42, -85957.92) * mm});
            skLineSegment(sketch, "E213", {"start": v(26461.4, -85154.37) * mm, "end": v(26270.87, -85944.52) * mm});
            skArc(sketch, "E214", {"start": v(26270.87, -85944.52) * mm, "mid": v(26927.99, -85819.92) * mm, "end": v(27269.18, -85244.65) * mm, "construction": true});
            skLineSegment(sketch, "E215", {"start": v(25363.43, -85725.7) * mm, "end": v(25474.54, -85752.5) * mm});
            skLineSegment(sketch, "E216", {"start": v(25553.97, -84935.55) * mm, "end": v(25665.08, -84962.34) * mm});
            skLineSegment(sketch, "E217.trimOffspring", {"start": v(25363.43, -85725.7) * mm, "end": v(24863.26, -87799.85) * mm});
            skLineSegment(sketch, "E218.trimOffspring", {"start": v(25474.54, -85752.5) * mm, "end": v(24974.37, -87826.64) * mm});
            skLineSegment(sketch, "E219", {"start": v(24733.67, -87037.01) * mm, "end": v(25029.98, -87108.46) * mm, "construction": true});
            skLineSegment(sketch, "E220", {"start": v(23543.8, -86932.98) * mm, "end": v(23758.16, -86044.06) * mm});
            skLineSegment(sketch, "E221", {"start": v(20717.84, -88250.3) * mm, "end": v(21532.68, -88446.8) * mm, "construction": true});
            skLineSegment(sketch, "E222", {"start": v(14201.72, -86992.5) * mm, "end": v(15773.69, -80473.77) * mm});
            skLineSegment(sketch, "E223", {"start": v(15063.1, -83908.09) * mm, "end": v(19470.65, -84970.95) * mm});
            skLineSegment(sketch, "E224", {"start": v(19739.1, -86133.06) * mm, "end": v(19238.93, -88207.2) * mm});
            skLineSegment(sketch, "E225", {"start": v(19470.65, -84970.95) * mm, "end": v(19247.36, -85896.9) * mm});
            skLineSegment(sketch, "E226.trimOffspring", {"start": v(19850.22, -86159.86) * mm, "end": v(19350.05, -88234) * mm});
            skLineSegment(sketch, "E227.trimOffspring", {"start": v(19850.22, -86159.86) * mm, "end": v(23405.9, -87017.3) * mm});
            skLineSegment(sketch, "E228", {"start": v(15036.3, -84019.2) * mm, "end": v(19332.74, -85055.27) * mm});
            skLineSegment(sketch, "E229", {"start": v(19332.74, -85055.27) * mm, "end": v(19109.45, -85981.23) * mm});
            skLineSegment(sketch, "E230", {"start": v(23000.54, -90486.03) * mm, "end": v(23286.35, -89300.8) * mm});
            skLineSegment(sketch, "E231", {"start": v(20809.72, -93720.17) * mm, "end": v(20738.27, -94016.47) * mm});
            skLineSegment(sketch, "E232", {"start": v(21698.64, -93934.53) * mm, "end": v(21627.2, -94230.83) * mm});
            skLineSegment(sketch, "E233", {"start": v(20774, -93868.32) * mm, "end": v(21662.92, -94082.68) * mm});
            skLineSegment(sketch, "E234", {"start": v(18295.67, -84805.18) * mm, "end": v(18152.76, -85397.8) * mm});
            skLineSegment(sketch, "E235", {"start": v(18152.76, -85397.8) * mm, "end": v(15486, -84754.72) * mm});
            skLineSegment(sketch, "E236", {"start": v(15486, -84754.72) * mm, "end": v(15048.36, -86569.6) * mm});
            skLineSegment(sketch, "E237", {"start": v(15048.36, -86569.6) * mm, "end": v(18789.23, -87471.7) * mm});
            skLineSegment(sketch, "E238", {"start": v(18789.23, -87471.7) * mm, "end": v(19146.5, -85990.16) * mm});
            skLineSegment(sketch, "E239", {"start": v(18396.54, -84711.93) * mm, "end": v(18369.75, -84823.05) * mm});
            skLineSegment(sketch, "E240", {"start": v(19285.46, -84926.3) * mm, "end": v(19258.67, -85037.4) * mm});
            skLineSegment(sketch, "E241", {"start": v(18383.14, -84767.49) * mm, "end": v(19272.06, -84981.85) * mm});
            skArc(sketch, "E242", {"start": v(18383.14, -84767.49) * mm, "mid": v(18512.5, -85490.95) * mm, "end": v(19132.53, -85885.54) * mm, "construction": true});
            skArc(sketch, "E243", {"start": v(24399.08, -89020.44) * mm, "mid": v(25122.55, -88891.09) * mm, "end": v(25517.13, -88271.06) * mm, "construction": true});
            skArc(sketch, "E244", {"start": v(26972.33, -93220.52) * mm, "mid": v(27417.21, -92635.53) * mm, "end": v(28148.94, -92566.91) * mm, "construction": true});
            skArc(sketch, "E245", {"start": v(21678.5, -86541.95) * mm, "mid": v(21370.68, -86938.03) * mm, "end": v(20870.02, -86969.15) * mm, "construction": true});
            skLineSegment(sketch, "E246", {"start": v(28435.5, -91378.6) * mm, "end": v(27052.74, -91045.15) * mm});
            skLineSegment(sketch, "E247", {"start": v(26412.84, -90773.26) * mm, "end": v(25933.51, -92760.99) * mm});
            skLineSegment(sketch, "E248", {"start": v(25822.4, -92734.2) * mm, "end": v(26301.73, -90746.47) * mm});
            skLineSegment(sketch, "E249", {"start": v(27079.53, -90934.03) * mm, "end": v(28462.3, -91267.48) * mm});
            skLineSegment(sketch, "E250", {"start": v(27872.16, -88838.96) * mm, "end": v(27401.76, -90789.65) * mm});
            skLineSegment(sketch, "E251", {"start": v(27401.76, -90789.65) * mm, "end": v(28512.9, -91057.6) * mm});
            skLineSegment(sketch, "E252", {"start": v(27694.73, -91199.96) * mm, "end": v(27444.65, -92237.04) * mm});
            skLineSegment(sketch, "E253", {"start": v(27444.65, -92237.04) * mm, "end": v(27987.88, -92368.03) * mm});
            skLineSegment(sketch, "E254", {"start": v(27987.88, -92368.03) * mm, "end": v(28237.96, -91330.96) * mm});
            skLineSegment(sketch, "E255", {"start": v(27798.08, -88821.1) * mm, "end": v(27530.13, -89932.25) * mm});
            skLineSegment(sketch, "E256", {"start": v(27530.13, -89932.25) * mm, "end": v(25579.45, -89461.85) * mm});
            skLineSegment(sketch, "E257", {"start": v(25579.45, -89461.85) * mm, "end": v(25847.4, -88350.7) * mm});
            skLineSegment(sketch, "E258", {"start": v(27497.2, -91152.33) * mm, "end": v(27306.65, -91942.48) * mm});
            skLineSegment(sketch, "E259", {"start": v(27306.65, -91942.48) * mm, "end": v(26936.27, -91853.16) * mm});
            skLineSegment(sketch, "E260", {"start": v(26936.27, -91853.16) * mm, "end": v(27126.81, -91063.01) * mm});
            skLineSegment(sketch, "E261", {"start": v(24281.04, -90376.77) * mm, "end": v(26256.41, -90853.12) * mm});
            skLineSegment(sketch, "E262", {"start": v(26256.41, -90853.12) * mm, "end": v(25803.88, -92729.73) * mm});
            skLineSegment(sketch, "E263", {"start": v(27079.53, -90934.03) * mm, "end": v(27052.74, -91045.15) * mm});
            skLineSegment(sketch, "E264", {"start": v(26301.73, -90746.47) * mm, "end": v(26412.84, -90773.26) * mm});
            skLineSegment(sketch, "E265", {"start": v(13369.06, -90933.02) * mm, "end": v(13665.37, -91004.47) * mm});
            skLineSegment(sketch, "E266", {"start": v(14012.14, -88266.26) * mm, "end": v(14308.45, -88337.71) * mm});
            skLineSegment(sketch, "E267", {"start": v(14160.3, -88301.99) * mm, "end": v(13517.22, -90968.74) * mm});
            skLineSegment(sketch, "E268", {"start": v(30171.65, -79438.68) * mm, "end": v(31071.07, -80909.72) * mm});
            skLineSegment(sketch, "E269", {"start": v(30928.16, -81502.33) * mm, "end": v(30236.78, -81335.6) * mm});
            skLineSegment(sketch, "E270", {"start": v(30236.78, -81335.6) * mm, "end": v(29879.52, -82817.14) * mm});
            skLineSegment(sketch, "E271", {"start": v(29879.52, -82817.14) * mm, "end": v(30570.9, -82983.86) * mm});
            skLineSegment(sketch, "E272", {"start": v(25090.54, -81819.07) * mm, "end": v(25201.65, -81845.86) * mm});
            skLineSegment(sketch, "E273", {"start": v(25376.35, -80633.84) * mm, "end": v(25487.47, -80660.63) * mm});
            skLineSegment(sketch, "E274", {"start": v(24998.85, -83011.91) * mm, "end": v(25025.65, -82900.8) * mm});
            skLineSegment(sketch, "E275", {"start": v(25887.77, -83226.27) * mm, "end": v(25914.57, -83115.16) * mm});
            skLineSegment(sketch, "E276", {"start": v(25012.25, -82956.35) * mm, "end": v(25901.17, -83170.71) * mm});
            skArc(sketch, "E277", {"start": v(25901.17, -83170.71) * mm, "mid": v(25771.81, -82447.25) * mm, "end": v(25151.79, -82052.66) * mm, "construction": true});
            skLineSegment(sketch, "E278", {"start": v(28653.3, -83893.16) * mm, "end": v(28680.1, -83782.05) * mm});
            skLineSegment(sketch, "E279", {"start": v(29420.86, -83960.68) * mm, "end": v(29394.06, -84071.8) * mm});
            skLineSegment(sketch, "E280", {"start": v(30161.62, -84139.31) * mm, "end": v(30134.83, -84250.43) * mm});
            skLineSegment(sketch, "E281", {"start": v(28666.7, -83837.6) * mm, "end": v(29407.46, -84016.24) * mm});
            skLineSegment(sketch, "E282", {"start": v(29407.46, -84016.24) * mm, "end": v(30148.23, -84194.87) * mm});
            skLineSegment(sketch, "E283", {"start": v(26761.5, -78302.8) * mm, "end": v(26690.05, -78599.1) * mm});
            skLineSegment(sketch, "E284", {"start": v(27502.27, -78481.43) * mm, "end": v(27430.82, -78777.74) * mm});
            skLineSegment(sketch, "E285", {"start": v(27798.58, -78552.88) * mm, "end": v(27727.13, -78849.2) * mm});
            skLineSegment(sketch, "E286", {"start": v(28539.35, -78731.52) * mm, "end": v(28467.9, -79027.82) * mm});
            skLineSegment(sketch, "E287", {"start": v(28835.65, -78802.97) * mm, "end": v(28764.2, -79099.28) * mm});
            skLineSegment(sketch, "E288", {"start": v(29576.42, -78981.6) * mm, "end": v(29504.96, -79277.9) * mm});
            skLineSegment(sketch, "E289", {"start": v(27466.55, -78629.58) * mm, "end": v(26725.78, -78450.95) * mm});
            skLineSegment(sketch, "E290", {"start": v(27762.85, -78701.04) * mm, "end": v(28503.62, -78879.67) * mm});
            skLineSegment(sketch, "E291", {"start": v(28799.93, -78951.12) * mm, "end": v(29540.7, -79129.76) * mm});
            skLineSegment(sketch, "E292", {"start": v(26511.22, -82266.17) * mm, "end": v(26296.86, -83155.09) * mm});
            skLineSegment(sketch, "E293", {"start": v(26296.86, -83155.09) * mm, "end": v(28222.85, -83619.53) * mm});
            skLineSegment(sketch, "E294", {"start": v(28222.85, -83619.53) * mm, "end": v(28437.2, -82730.61) * mm});
            skLineSegment(sketch, "E295", {"start": v(28437.2, -82730.61) * mm, "end": v(26511.22, -82266.17) * mm});
            skLineSegment(sketch, "E296", {"start": v(27492.99, -78844.99) * mm, "end": v(29418.98, -79309.43) * mm});
            skLineSegment(sketch, "E297", {"start": v(29418.98, -79309.43) * mm, "end": v(29204.62, -80198.35) * mm});
            skLineSegment(sketch, "E298", {"start": v(29204.62, -80198.35) * mm, "end": v(27278.63, -79733.9) * mm});
            skLineSegment(sketch, "E299", {"start": v(27278.63, -79733.9) * mm, "end": v(27492.99, -78844.99) * mm});
            skLineSegment(sketch, "E300", {"start": v(25456.74, -80300.5) * mm, "end": v(25567.85, -80327.29) * mm});
            skLineSegment(sketch, "E301", {"start": v(25671.1, -79411.58) * mm, "end": v(25782.21, -79438.37) * mm});
            skLineSegment(sketch, "E302", {"start": v(25885.45, -78522.66) * mm, "end": v(25996.57, -78549.45) * mm});
            skLineSegment(sketch, "E303", {"start": v(25941.01, -78536.05) * mm, "end": v(25726.65, -79424.97) * mm});
            skLineSegment(sketch, "E304", {"start": v(25726.65, -79424.97) * mm, "end": v(25512.3, -80313.9) * mm});
            skLineSegment(sketch, "E305", {"start": v(14126.1, -76091.92) * mm, "end": v(14373.02, -76151.47) * mm});
            skLineSegment(sketch, "E306", {"start": v(14373.02, -76151.47) * mm, "end": v(13610.85, -79312.07) * mm});
            skLineSegment(sketch, "E307", {"start": v(13610.85, -79312.07) * mm, "end": v(13363.93, -79252.53) * mm});
            skLineSegment(sketch, "E308", {"start": v(13991.93, -77731.77) * mm, "end": v(13745.01, -77672.23) * mm});
            skLineSegment(sketch, "E309", {"start": v(13801.4, -78521.92) * mm, "end": v(13554.47, -78462.38) * mm});
            skLineSegment(sketch, "E310", {"start": v(14182.48, -76941.62) * mm, "end": v(13935.55, -76882.07) * mm});
            skLineSegment(sketch, "E311", {"start": v(18829.86, -78689.39) * mm, "end": v(18311.32, -78564.35) * mm});
            skLineSegment(sketch, "E312", {"start": v(18311.32, -78564.35) * mm, "end": v(18025.5, -79749.57) * mm});
            skLineSegment(sketch, "E313", {"start": v(18025.5, -79749.57) * mm, "end": v(18544.04, -79874.61) * mm});
            skLineSegment(sketch, "E314", {"start": v(14985.95, -75776.71) * mm, "end": v(14825.18, -76443.4) * mm});
            skLineSegment(sketch, "E315", {"start": v(14825.18, -76443.4) * mm, "end": v(19566.08, -77586.65) * mm});
            skLineSegment(sketch, "E316", {"start": v(19566.08, -77586.65) * mm, "end": v(19726.85, -76919.96) * mm});
            skLineSegment(sketch, "E317", {"start": v(17195.63, -77015.03) * mm, "end": v(17356.4, -76348.34) * mm});
            skLineSegment(sketch, "E318", {"start": v(16010.4, -76729.21) * mm, "end": v(16171.17, -76062.52) * mm});
            skLineSegment(sketch, "E319", {"start": v(18380.86, -77300.84) * mm, "end": v(18541.63, -76634.15) * mm});
            skLineSegment(sketch, "E320", {"start": v(13985.6, -79925) * mm, "end": v(14146.38, -79258.31) * mm});
            skLineSegment(sketch, "E321", {"start": v(14146.38, -79258.31) * mm, "end": v(17702.05, -80115.75) * mm});
            skLineSegment(sketch, "E322", {"start": v(17702.05, -80115.75) * mm, "end": v(17541.28, -80782.44) * mm});
            skLineSegment(sketch, "E323", {"start": v(15331.6, -79544.13) * mm, "end": v(15170.83, -80210.81) * mm});
            skLineSegment(sketch, "E324", {"start": v(16516.83, -79829.94) * mm, "end": v(16356.06, -80496.63) * mm});
            skSolve(sketch);
        }
        {
            var Q0;
            Q0=makeQuery(id+"F8.imprint","IMPRINT",FACE,{"disambiguationData":[TD([[makeQuery(id+"F8.imprint","IMPRINT",EDGE,{"derivedFrom":sQuery(id+"F8.wireOp",EDGE,"E27")}),1.0]])]});
            var Q1;
            {var subQ11=sQuery(id+"F8.wireOp",EDGE,"E50");Q1=makeQuery(id+"F8.imprint","IMPRINT",FACE,{"disambiguationData":[TD([[makeQuery(id+"F8.imprint","IMPRINT",EDGE,{"derivedFrom":subQ11}),-1.0]])]});}
            var Q2;
            {var subQ0=sQuery(id+"F8.wireOp",EDGE,"E65");Q2=makeQuery(id+"F8.imprint","IMPRINT",FACE,{"disambiguationData":[TD([[makeQuery(id+"F8.imprint","IMPRINT",EDGE,{"derivedFrom":subQ0}),-1.0]])]});}
            var Q3;
            {var subQ4=sQuery(id+"F8.wireOp",EDGE,"rclvcfd8-MIHF-olu5-eLjo-lo3ld7nkITQP");var subQ5=sQuery(id+"F8.wireOp",EDGE,"E61");var subQ6=makeQuery(id+"F8.imprint","INTERSECT",VERTEX,{"derivedFrom":[subQ5,subQ4]});Q3=makeQuery(id+"F8.imprint","IMPRINT",FACE,{"disambiguationData":[TD([[makeQuery(id+"F8.imprint","IMPRINT",EDGE,{"disambiguationData":[TD([[subQ6,-1.0]])],"derivedFrom":subQ5}),-1.0]])]});}
            var Q4;
            {var subQ0=sQuery(id+"F8.wireOp",EDGE,"E117");Q4=makeQuery(id+"F8.imprint","IMPRINT",FACE,{"disambiguationData":[TD([[makeQuery(id+"F8.imprint","IMPRINT",EDGE,{"derivedFrom":subQ0}),-1.0]])]});}
            var Q5;
            {var subQ0=sQuery(id+"F8.wireOp",EDGE,"E175");Q5=makeQuery(id+"F8.imprint","IMPRINT",FACE,{"disambiguationData":[TD([[makeQuery(id+"F8.imprint","IMPRINT",EDGE,{"derivedFrom":subQ0}),1.0]])]});}
            var Q6;
            {var subQ1=sQuery(id+"F8.wireOp",EDGE,"kQ18YiRS-KgXn-pTWU-JgMz-coXiSHkQz2KQ");Q6=makeQuery(id+"F8.imprint","IMPRINT",FACE,{"disambiguationData":[TD([[makeQuery(id+"F8.imprint","IMPRINT",EDGE,{"derivedFrom":subQ1}),-1.0]])]});}
            var Q7;
            {var subQ0=sQuery(id+"F8.wireOp",EDGE,"E173");Q7=makeQuery(id+"F8.imprint","IMPRINT",FACE,{"disambiguationData":[TD([[makeQuery(id+"F8.imprint","IMPRINT",EDGE,{"derivedFrom":subQ0}),-1.0]])]});}
            var Q8;
            {var subQ9=sQuery(id+"F8.wireOp",EDGE,"E114");Q8=makeQuery(id+"F8.imprint","IMPRINT",FACE,{"disambiguationData":[TD([[makeQuery(id+"F8.imprint","IMPRINT",EDGE,{"derivedFrom":subQ9}),1.0]])]});}
            var Q9;
            {var subQ5=sQuery(id+"F8.wireOp",EDGE,"GEOfW8i7-v1bV-P7JK-g7ps-RluW9onRIqib");Q9=makeQuery(id+"F8.imprint","IMPRINT",FACE,{"disambiguationData":[TD([[makeQuery(id+"F8.imprint","IMPRINT",EDGE,{"derivedFrom":subQ5}),1.0]])]});}
            var Q10;
            {var subQ0=sQuery(id+"F8.wireOp",EDGE,"E120");var subQ1=sQuery(id+"F8.wireOp",EDGE,"E115");var subQ2=makeQuery(id+"F8.imprint","INTERSECT",VERTEX,{"derivedFrom":[subQ1,subQ0]});Q10=makeQuery(id+"F8.imprint","IMPRINT",FACE,{"disambiguationData":[TD([[makeQuery(id+"F8.imprint","IMPRINT",EDGE,{"disambiguationData":[TD([[subQ2,1.0]])],"derivedFrom":subQ1}),1.0]])]});}
            var Q11;
            {var subQ0=sQuery(id+"F8.wireOp",EDGE,"E120");var subQ5=sQuery(id+"F8.wireOp",EDGE,"DJspllXv-pb2S-FSFw-zfOf-plQMQFauy2Zp");var subQ10=makeQuery(id+"F8.imprint","INTERSECT",VERTEX,{"derivedFrom":[subQ5,subQ0]});Q11=makeQuery(id+"F8.imprint","IMPRINT",FACE,{"disambiguationData":[TD([[makeQuery(id+"F8.imprint","IMPRINT",EDGE,{"disambiguationData":[TD([[subQ10,-1.0]])],"derivedFrom":subQ5}),1.0]])]});}
            var Q12;
            {var subQ0=sQuery(id+"F8.wireOp",EDGE,"E124");var subQ1=sQuery(id+"F8.wireOp",EDGE,"E121");var subQ2=makeQuery(id+"F8.imprint","INTERSECT",VERTEX,{"derivedFrom":[subQ1,subQ0]});Q12=makeQuery(id+"F8.imprint","IMPRINT",FACE,{"disambiguationData":[TD([[makeQuery(id+"F8.imprint","IMPRINT",EDGE,{"disambiguationData":[TD([[subQ2,-1.0]])],"derivedFrom":subQ1}),-1.0]])]});}
            var Q13;
            {var subQ0=sQuery(id+"F8.wireOp",EDGE,"E122");var subQ1=sQuery(id+"F8.wireOp",EDGE,"E121");var subQ2=makeQuery(id+"F8.imprint","INTERSECT",VERTEX,{"derivedFrom":[subQ1,subQ0]});Q13=makeQuery(id+"F8.imprint","IMPRINT",FACE,{"disambiguationData":[TD([[makeQuery(id+"F8.imprint","IMPRINT",EDGE,{"disambiguationData":[TD([[subQ2,1.0]])],"derivedFrom":subQ1}),-1.0]])]});}
            var Q14;
            {var subQ1=sQuery(id+"F8.wireOp",EDGE,"E67");var subQ6=sQuery(id+"F8.wireOp",EDGE,"E124");var subQ7=makeQuery(id+"F8.imprint","INTERSECT",VERTEX,{"derivedFrom":[subQ1,subQ6]});Q14=makeQuery(id+"F8.imprint","IMPRINT",FACE,{"disambiguationData":[TD([[makeQuery(id+"F8.imprint","IMPRINT",EDGE,{"disambiguationData":[TD([[subQ7,1.0]])],"derivedFrom":subQ1}),-1.0]])]});}
            var Q15;
            {var subQ4=sQuery(id+"F8.wireOp",EDGE,"E123");var subQ5=sQuery(id+"F8.wireOp",EDGE,"E67");var subQ6=makeQuery(id+"F8.imprint","INTERSECT",VERTEX,{"derivedFrom":[subQ5,subQ4]});Q15=makeQuery(id+"F8.imprint","IMPRINT",FACE,{"disambiguationData":[TD([[makeQuery(id+"F8.imprint","IMPRINT",EDGE,{"disambiguationData":[TD([[subQ6,-1.0]])],"derivedFrom":subQ4}),-1.0]])]});}
            var Q16;
            {var subQ16=sQuery(id+"F8.wireOp",EDGE,"E58.0");Q16=makeQuery(id+"F8.imprint","IMPRINT",FACE,{"disambiguationData":[TD([[makeQuery(id+"F8.imprint","IMPRINT",EDGE,{"derivedFrom":subQ16}),1.0]])]});}
            extrude(context, id + "F9", {"entities" : qUnion([Q0, Q1, Q2, Q3, Q4, Q5, Q6, Q7, Q8, Q9, Q10, Q11, Q12, Q13, Q14, Q15, Q16]), "operationType" : NewBodyOperationType.ADD, "depth" : 3048 * mm, "offsetDistance" : 25.4 * mm});
        }
    });
